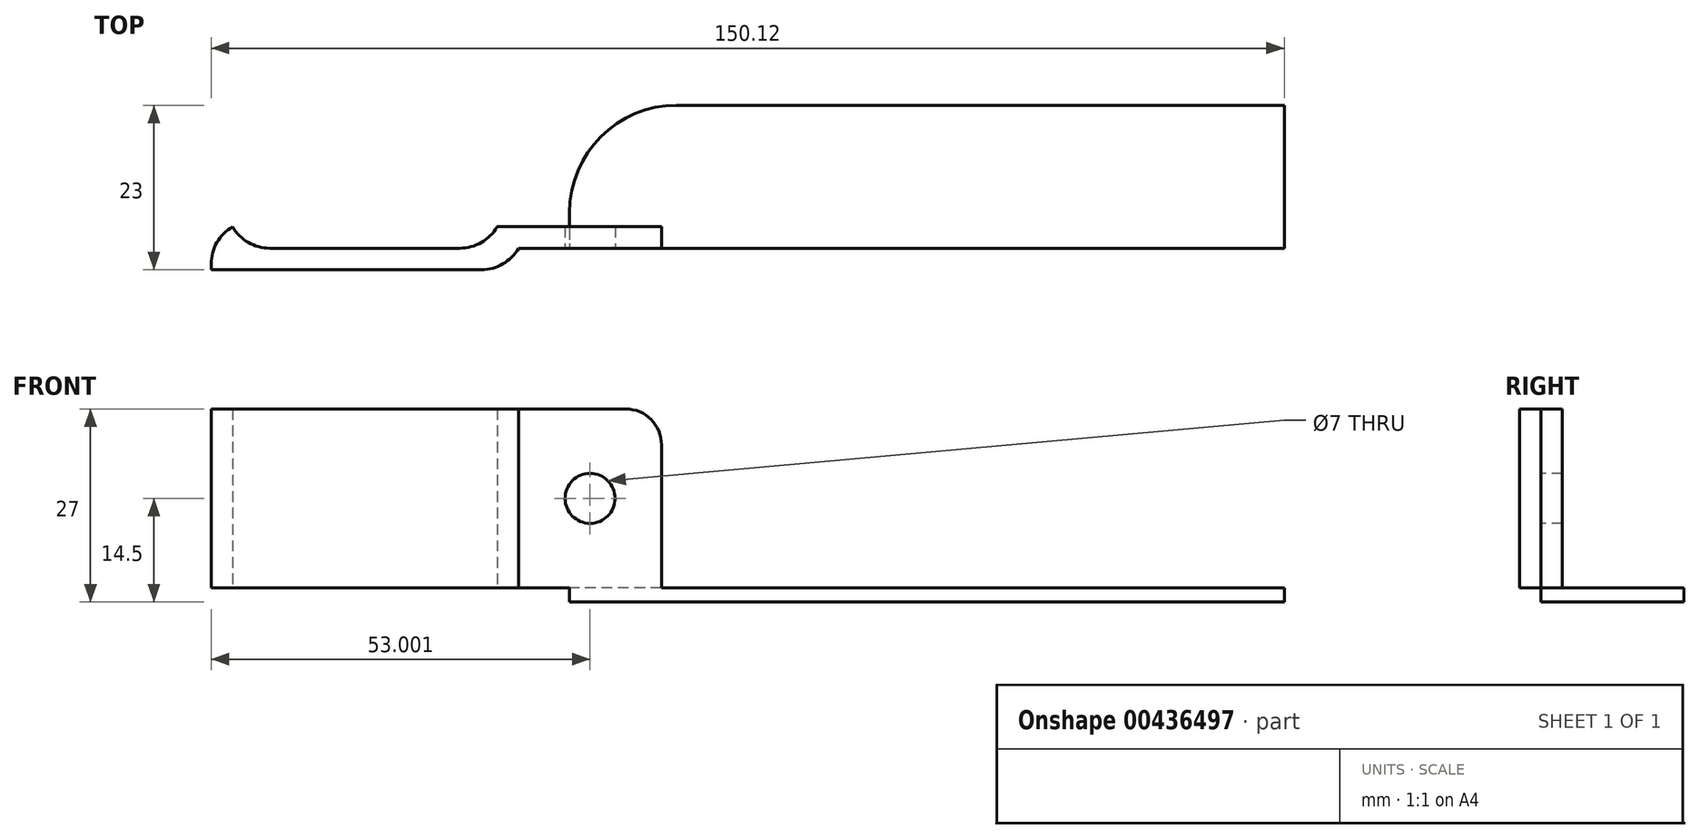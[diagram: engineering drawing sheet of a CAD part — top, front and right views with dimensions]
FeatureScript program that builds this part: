
annotation { "Feature Type Name" : "Feature", "Feature Type Description" : "" }
export const myFeature = defineFeature(function(context is Context, id is Id, definition is map)
    precondition{}
    {
        {
            var Q0;
            Q0=qCreatedBy(makeId("Top.planeOp"),FACE);
            var sketch = newSketch(context, id + "F0", { "sketchPlane" : qUnion([Q0])});
            skLineSegment(sketch, "E0.bottom", {"start": v(-3.34, -52.78) * mm, "end": v(96.66, -52.78) * mm});
            skLineSegment(sketch, "E0.top", {"start": v(-3.34, -72.78) * mm, "end": v(96.66, -72.78) * mm});
            skLineSegment(sketch, "E0.left", {"start": v(-3.34, -52.78) * mm, "end": v(-3.34, -72.78) * mm});
            skLineSegment(sketch, "E0.right", {"start": v(96.66, -52.78) * mm, "end": v(96.66, -72.78) * mm});
            skSolve(sketch);
        }
        {
            var Q0;
            Q0=makeQuery(id+"F0.imprint","IMPRINT",FACE,{"disambiguationData":[TD([[makeQuery(id+"F0.imprint","IMPRINT",EDGE,{"derivedFrom":sQuery(id+"F0.wireOp",EDGE,"E0.bottom")}),-1.0]])]});
            extrude(context, id + "F1", {"entities" : qUnion([Q0]), "depth" : 2 * mm});
        }
        {
            var Q0;
            Q0=makeQuery(id+"F1.opExtrude","SWEPT_EDGE",EDGE,{"disambiguationData":[OSD([sQuery(id+"F0.wireOp",EDGE,"E0.bottom"),sQuery(id+"F0.wireOp",EDGE,"E0.left")])]});
            fillet(context, id + "F2", {"entities" : qUnion([Q0]), "radius" : 15 * mm, "tangentPropagation" : true, "allowEdgeOverflow" : false});
        }
        {
            var Q0;
            Q0=makeQuery(id+"F1.opExtrude","CAP_FACE",FACE,{"disambiguationData":[OSD([sQuery(id+"F0.wireOp",EDGE,"E0.bottom"),sQuery(id+"F0.wireOp",EDGE,"E0.top"),sQuery(id+"F0.wireOp",EDGE,"E0.left"),sQuery(id+"F0.wireOp",EDGE,"E0.right")])],"isStart":false});
            var sketch = newSketch(context, id + "F3", { "sketchPlane" : qUnion([Q0])});
            skLineSegment(sketch, "E1.bottom", {"start": v(9.54, -72.78) * mm, "end": v(-10.46, -72.78) * mm});
            skLineSegment(sketch, "E1.top", {"start": v(9.54, -69.78) * mm, "end": v(-10.46, -69.78) * mm});
            skLineSegment(sketch, "E1.left", {"start": v(9.54, -72.78) * mm, "end": v(9.54, -69.78) * mm});
            skLineSegment(sketch, "E2.bottom", {"start": v(-10.46, -69.78) * mm, "end": v(-13.46, -69.78) * mm});
            skLineSegment(sketch, "E2.top", {"start": v(-10.46, -75.78) * mm, "end": v(-13.46, -75.78) * mm});
            skLineSegment(sketch, "E2.left", {"start": v(-10.46, -72.78) * mm, "end": v(-10.46, -75.78) * mm});
            skLineSegment(sketch, "E2.right", {"start": v(-13.46, -69.78) * mm, "end": v(-13.46, -72.78) * mm});
            skLineSegment(sketch, "E3.bottom", {"start": v(-13.46, -72.78) * mm, "end": v(-50.46, -72.78) * mm});
            skLineSegment(sketch, "E3.top", {"start": v(-13.46, -75.78) * mm, "end": v(-53.46, -75.78) * mm});
            skLineSegment(sketch, "E3.right", {"start": v(-53.46, -72.78) * mm, "end": v(-53.46, -75.78) * mm});
            skLineSegment(sketch, "E4.bottom", {"start": v(-53.46, -75.78) * mm, "end": v(-50.46, -75.78) * mm});
            skLineSegment(sketch, "E4.top", {"start": v(-53.46, -69.78) * mm, "end": v(-50.46, -69.78) * mm});
            skLineSegment(sketch, "E4.left", {"start": v(-53.46, -75.78) * mm, "end": v(-53.46, -69.78) * mm});
            skLineSegment(sketch, "E4.right", {"start": v(-50.46, -72.78) * mm, "end": v(-50.46, -69.78) * mm});
            skSolve(sketch);
        }
        {
            var Q0;
            Q0 = qSketchRegion(id + "F3", true);
            extrude(context, id + "F4", {"entities" : qUnion([Q0]), "operationType" : NewBodyOperationType.ADD, "depth" : 25 * mm});
        }
        {
            var Q0;
            Q0=makeQuery(id+"F4.opExtrude","SWEPT_EDGE",EDGE,{"disambiguationData":[OSD([sQuery(id+"F3.wireOp",EDGE,"E2.top"),sQuery(id+"F3.wireOp",EDGE,"E2.left")])]});
            var Q1;
            Q1=makeQuery(id+"F4.opExtrude","SWEPT_EDGE",EDGE,{"disambiguationData":[OSD([sQuery(id+"F3.wireOp",EDGE,"E2.right"),sQuery(id+"F3.wireOp",EDGE,"E3.bottom")])]});
            var Q2;
            Q2=makeQuery(id+"F4.opExtrude","SWEPT_EDGE",EDGE,{"disambiguationData":[OSD([sQuery(id+"F3.wireOp",EDGE,"E4.top"),sQuery(id+"F3.wireOp",EDGE,"E4.left")])]});
            var Q3;
            Q3=makeQuery(id+"F4.opExtrude","SWEPT_EDGE",EDGE,{"disambiguationData":[OSD([sQuery(id+"F3.wireOp",EDGE,"E3.bottom"),sQuery(id+"F3.wireOp",EDGE,"E4.right")])]});
            var Q4;
            Q4=makeQuery(id+"F4.opExtrude","SWEPT_EDGE",EDGE,{"disambiguationData":[OSD([sQuery(id+"F3.wireOp",EDGE,"E4.bottom"),sQuery(id+"F3.wireOp",EDGE,"E4.left")])]});
            fillet(context, id + "F5", {"entities" : qUnion([Q0, Q1, Q2, Q3, Q4]), "radius" : 6 * mm, "tangentPropagation" : true, "allowEdgeOverflow" : false});
        }
        {
            var Q0;
            Q0=makeQuery(id+"F4.opExtrude","CAP_EDGE",EDGE,{"disambiguationData":[OSD([sQuery(id+"F3.wireOp",EDGE,"E1.left")])],"isStart":false});
            fillet(context, id + "F6", {"entities" : qUnion([Q0]), "radius" : 5 * mm, "tangentPropagation" : true, "allowEdgeOverflow" : false});
        }
        {
            var Q0;
            Q0=makeQuery(id+"F4.boolean.opBoolean","MERGE",FACE,{"derivedFrom":[makeQuery(id+"F1.opExtrude","SWEPT_FACE",FACE,{"disambiguationData":[OSD([sQuery(id+"F0.wireOp",EDGE,"E0.top")])]}),makeQuery(id+"F4.opExtrude","SWEPT_FACE",FACE,{"disambiguationData":[OSD([sQuery(id+"F3.wireOp",EDGE,"E1.bottom")])]})]});
            var sketch = newSketch(context, id + "F7", { "sketchPlane" : qUnion([Q0])});
            skPoint(sketch, "E5", {"position": v(-0.46, 14.5) * mm});
            skSolve(sketch);
        }
        {
            var Q0;
            Q0=sQuery(id+"F7.wireOp",VERTEX,"E5");
            var Q1;
            Q1=makeQuery(id+"F1.opExtrude","SWEPT_BODY",BODY,{"disambiguationData":[OSD([sQuery(id+"F0.wireOp",EDGE,"E0.bottom"),sQuery(id+"F0.wireOp",EDGE,"E0.top"),sQuery(id+"F0.wireOp",EDGE,"E0.left"),sQuery(id+"F0.wireOp",EDGE,"E0.right")])]});
            hole(context, id + "F8", {"style" : HoleStyle.SIMPLE, "endStyle" : HoleEndStyle.THROUGH, "holeDiameter" : 7 * mm, "isTappedThrough" : true, "tappedDepth" : 12 * mm, "tapClearance" : 3, "locations" : qUnion([Q0]), "scope" : qUnion([Q1])});
        }
    });
